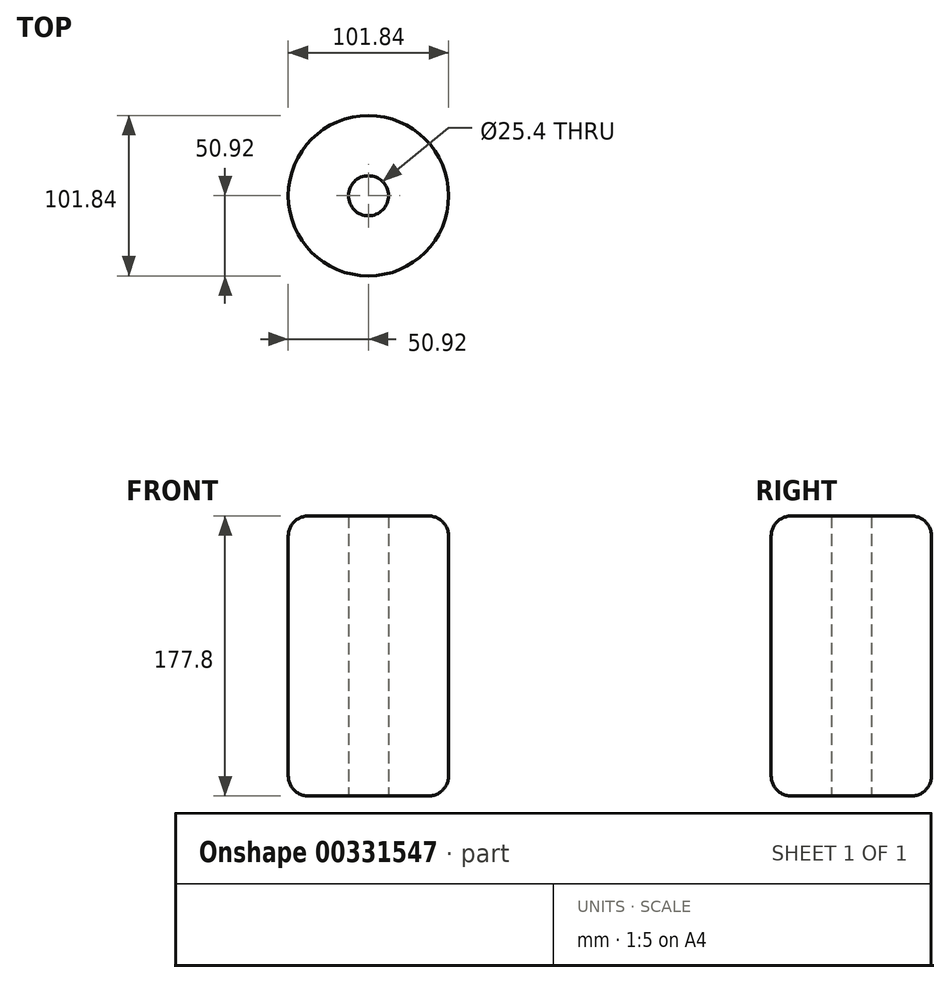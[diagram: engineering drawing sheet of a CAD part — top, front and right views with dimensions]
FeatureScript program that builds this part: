
annotation { "Feature Type Name" : "Feature", "Feature Type Description" : "" }
export const myFeature = defineFeature(function(context is Context, id is Id, definition is map)
    precondition{}
    {
        {
            var Q0;
            Q0=qCreatedBy(makeId("Top.planeOp"),FACE);
            var sketch = newSketch(context, id + "F0", { "sketchPlane" : qUnion([Q0])});
            skCircle(sketch, "E0", {"center": v(0, 0) * mm, "radius": 50.92 * mm});
            skSolve(sketch);
        }
        {
            var Q0;
            Q0=makeQuery(id+"F0.imprint","IMPRINT",FACE,{"disambiguationData":[TD([[makeQuery(id+"F0.imprint","IMPRINT",EDGE,{"derivedFrom":sQuery(id+"F0.wireOp",EDGE,"E0")}),1.0]])]});
            extrude(context, id + "F1", {"entities" : qUnion([Q0]), "depth" : 177.8 * mm});
        }
        {
            var Q0;
            Q0=makeQuery(id+"F1.opExtrude","CAP_EDGE",EDGE,{"disambiguationData":[OSD([sQuery(id+"F0.wireOp",EDGE,"E0")])],"isStart":true});
            var Q1;
            Q1=makeQuery(id+"F1.opExtrude","CAP_EDGE",EDGE,{"disambiguationData":[OSD([sQuery(id+"F0.wireOp",EDGE,"E0")])],"isStart":false});
            fillet(context, id + "F2", {"entities" : qUnion([Q0, Q1]), "radius" : 12.7 * mm, "tangentPropagation" : true, "allowEdgeOverflow" : false});
        }
        {
            var Q0;
            Q0=makeQuery(id+"F1.opExtrude","CAP_FACE",FACE,{"disambiguationData":[OSD([sQuery(id+"F0.wireOp",EDGE,"E0")])],"isStart":true});
            var sketch = newSketch(context, id + "F3", { "sketchPlane" : qUnion([Q0])});
            skSolve(sketch);
        }
        {
            var Q0;
            {var subQ0=sQuery(id+"F0.wireOp",EDGE,"E0");Q0=makeQuery(id+"F3.imprint","IMPRINT",FACE,{"disambiguationData":[TD([[makeQuery(id+"F3.imprint","IMPRINT",EDGE,{"derivedFrom":makeQuery(id+"F2.opFillet","BLEND_EDGE",EDGE,{"blendedFrom":[makeQuery(id+"F1.opExtrude","CAP_EDGE",EDGE,{"disambiguationData":[OSD([subQ0])],"isStart":true}),makeQuery(id+"F1.opExtrude","CAP_FACE",FACE,{"disambiguationData":[OSD([subQ0])],"isStart":true})],"blendedInto":[makeQuery(id+"F1.opExtrude","CAP_FACE",FACE,{"disambiguationData":[OSD([subQ0])],"isStart":true})]})}),1.0]])]});}
            var sketch = newSketch(context, id + "F4", { "sketchPlane" : qUnion([Q0])});
            skCircle(sketch, "E1", {"center": v(0, 0) * mm, "radius": 20.58 * mm});
            skSolve(sketch);
        }
        {
            var Q0;
            Q0=sQuery(id+"F4.wireOp",VERTEX,"E1.center");
            var Q1;
            Q1=makeQuery(id+"F1.opExtrude","SWEPT_BODY",BODY,{"disambiguationData":[OSD([sQuery(id+"F0.wireOp",EDGE,"E0")])]});
            hole(context, id + "F5", {"style" : HoleStyle.SIMPLE, "endStyle" : HoleEndStyle.BLIND, "holeDiameter" : 25.4 * mm, "holeDepth" : 177.8 * mm, "tappedDepth" : 12.7 * mm, "tapClearance" : 3, "startFromSketch" : true, "locations" : qUnion([Q0]), "scope" : qUnion([Q1])});
        }
    });
